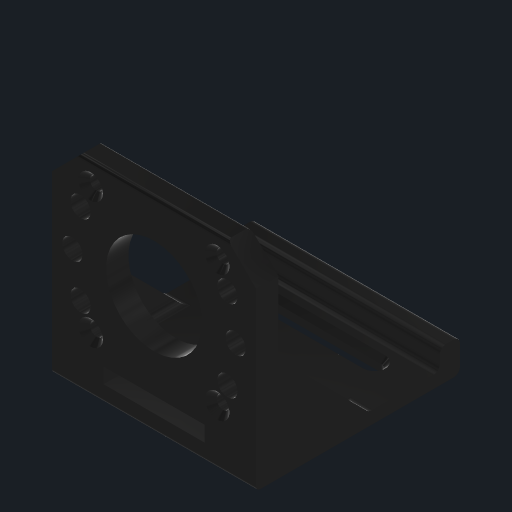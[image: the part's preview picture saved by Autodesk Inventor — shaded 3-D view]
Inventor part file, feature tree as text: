
AUTODESK INVENTOR PART (.ipt)
format: ipt  version: 2023 (Build 270158000, 158)  size: 316,928 bytes
history: native  units: mm
features: sketch x5, extrude x5, fillet x4, chamfer x2, mirror x1, hole x1, projected_geometry x1
ambient origin geometry x8: Origin, YZ Plane, XZ Plane, XY Plane, X Axis, Y Axis, Z Axis, Center Point
bodies: Solid1 (feature_tree)
feature tree (19):
  sketch  "Sketch1"  dims[d0=42.0mm d1=42.0mm d2=31.0mm d3=3.2mm d4=3.2mm d5=23.5mm d7=5.5mm d8=0.0mm]
  extrude  "Extrusion1"  Depth=3.2mm TaperAngle=0.0deg
  extrude  "Extrusion2"  Depth=4.0mm
  extrude  "Extrusion3"  Depth=50.0mm
  mirror  "Mirror1"
  fillet  "Fillet1"  Radius=3.0mm
  fillet  "Fillet2"  [1 undecoded]
  extrude  "Extrusion4"  Depth=2.0mm
  fillet  "Fillet3"  Radius=0.4mm
  extrude  "Extrusion5"  Depth=2.0mm TaperAngle=0.0deg
  hole  "Hole2"  [1 undecoded]
  chamfer  "Chamfer1"  Distance=5.0mm
  fillet  "Fillet4"  Radius=1.6mm
  chamfer  "Chamfer2"  Distance=1.6mm
  sketch  "Sketch2"  dims[d9=4.0mm d10=4.0mm]
  sketch  "Sketch5"  dims[d11=5.0mm d12=50.0mm d15=3.0mm d16=0.0mm d20=45.0deg]
  sketch  "Sketch6"  dims[d21=3.5mm d22=0.0mm d23=2.0mm d24=0.4mm]
  sketch  "Sketch8"  dims[d25=5.0mm d26=5.0mm d27=0.0mm d28=1.5mm d43=5.0mm d44=0.0mm d59=3.2mm d60=6.0mm d61=6.0mm d62=2.0mm d63=90.0deg d64=10.0mm d65=0.0mm d71=1.6mm d72=1.6mm d73=25.0mm d74=25.0mm d75=30.0mm d76=30.0mm d78=7.0mm d79=7.0mm d80=2.0mm d81=45.0deg d82=1.0mm d83=1.125mm d84=2.0mm d85=45.0deg d86=11.0mm d94=3.8mm d95=23.0mm d96=24.8mm d97=12.4mm d98=5.0mm d99=5.0mm d100=5.0mm d101=10.0mm d102=10.0mm d103=2.0mm d104=2.0mm d105=20.0mm]
  projected_geometry  "Projected Loop1"
note: 2 required parameter values undecoded (feature->parameter linkage not recoverable at this tier; creation-order binding heuristic only, values carry confidence <= 0.55)
